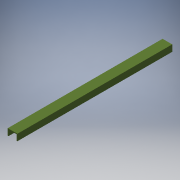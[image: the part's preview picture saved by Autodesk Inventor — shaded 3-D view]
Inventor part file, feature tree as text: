
AUTODESK INVENTOR PART (.ipt)
format: ipt  version: 2017 SP1 (Build 210196100, 196)  size: 126,464 bytes
history: native  units: in
note: dims shown in document units (in); Inventor stores cm internally (conversion verified against a paired STEP export)
features: extrude x2, sketch x2
ambient origin geometry x8: Origin, YZ Plane, XZ Plane, XY Plane, X Axis, Y Axis, Z Axis, Center Point
bodies: Solid1 (feature_tree)
feature tree (4):
  extrude  "Extrusion1"  Depth=1.25in
  extrude  "Extrusion2"  Depth=1.5in
  sketch  "Sketch1"  dims[d0=0.125in d1=1.25in]
  sketch  "Sketch2"  dims[d2=1.0in d3=1.5in d4=24.0in d5=0.0in d7=0.375in d8=0.5in d12=30.0in d13=0.0in d14=1.0in d15=0.25in d16=21.0in d17=0.375in d18=5.5in]
